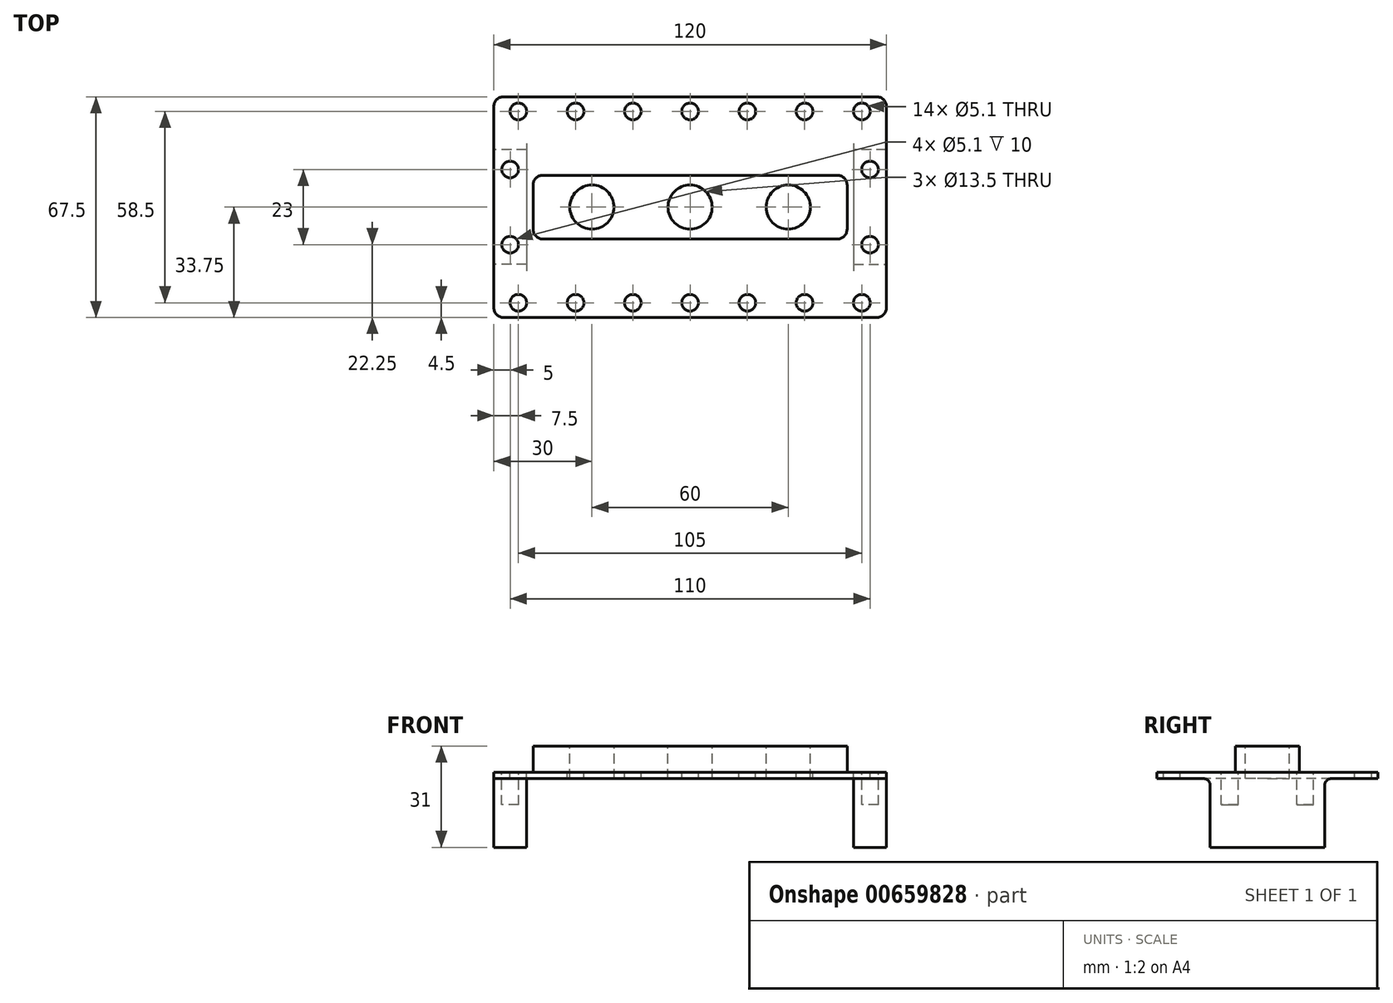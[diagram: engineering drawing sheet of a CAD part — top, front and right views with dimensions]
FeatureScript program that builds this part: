
annotation { "Feature Type Name" : "Feature", "Feature Type Description" : "" }
export const myFeature = defineFeature(function(context is Context, id is Id, definition is map)
    precondition{}
    {
        {
            var Q0;
            Q0=qCreatedBy(makeId("Top.planeOp"),FACE);
            var sketch = newSketch(context, id + "F0", { "sketchPlane" : qUnion([Q0])});
            skLineSegment(sketch, "E0.bottom", {"start": v(0, 0) * mm, "end": v(120, 0) * mm});
            skLineSegment(sketch, "E0.top", {"start": v(0, -67.5) * mm, "end": v(120, -67.5) * mm});
            skLineSegment(sketch, "E0.left", {"start": v(0, 0) * mm, "end": v(0, -67.5) * mm});
            skLineSegment(sketch, "E0.right", {"start": v(120, 0) * mm, "end": v(120, -67.5) * mm});
            skSolve(sketch);
        }
        {
            var Q0;
            Q0 = qSketchRegion(id + "F0", true);
            extrude(context, id + "F1", {"entities" : qUnion([Q0]), "depth" : 20 * mm, "offsetDistance" : 25 * mm});
        }
        {
            var Q0;
            Q0=makeQuery(id+"F1.opExtrude","CAP_FACE",FACE,{"disambiguationData":[OSD([sQuery(id+"F0.wireOp",EDGE,"E0.bottom"),sQuery(id+"F0.wireOp",EDGE,"E0.top"),sQuery(id+"F0.wireOp",EDGE,"E0.left"),sQuery(id+"F0.wireOp",EDGE,"E0.right")])],"isStart":false});
            var sketch = newSketch(context, id + "F2", { "sketchPlane" : qUnion([Q0])});
            skLineSegment(sketch, "E1.bottom", {"start": v(108, -43.5) * mm, "end": v(12, -43.5) * mm});
            skLineSegment(sketch, "E1.top", {"start": v(108, -24) * mm, "end": v(12, -24) * mm});
            skLineSegment(sketch, "E1.left", {"start": v(108, -43.5) * mm, "end": v(108, -24) * mm});
            skLineSegment(sketch, "E1.right", {"start": v(12, -43.5) * mm, "end": v(12, -24) * mm});
            skSolve(sketch);
        }
        {
            var Q0;
            Q0 = qSketchRegion(id + "F2", true);
            extrude(context, id + "F3", {"entities" : qUnion([Q0]), "operationType" : NewBodyOperationType.ADD, "depth" : 8 * mm, "offsetDistance" : 25 * mm});
        }
        {
            var Q0;
            Q0=makeQuery(id+"F3.opExtrude","CAP_FACE",FACE,{"disambiguationData":[OSD([sQuery(id+"F2.wireOp",EDGE,"E1.bottom"),sQuery(id+"F2.wireOp",EDGE,"E1.top"),sQuery(id+"F2.wireOp",EDGE,"E1.left"),sQuery(id+"F2.wireOp",EDGE,"E1.right")])],"isStart":false});
            var sketch = newSketch(context, id + "F4", { "sketchPlane" : qUnion([Q0])});
            skCircle(sketch, "E2", {"center": v(60, -33.75) * mm, "radius": 6.75 * mm});
            skCircle(sketch, "E3", {"center": v(30, -33.75) * mm, "radius": 6.75 * mm});
            skCircle(sketch, "E4", {"center": v(90, -33.75) * mm, "radius": 6.75 * mm});
            skSolve(sketch);
        }
        {
            var Q0;
            Q0 = qSketchRegion(id + "F4", true);
            extrude(context, id + "F5", {"entities" : qUnion([Q0]), "operationType" : NewBodyOperationType.REMOVE, "oppositeDirection" : true, "depth" : 25 * mm, "offsetDistance" : 25 * mm});
        }
        {
            var Q0;
            Q0=makeQuery(id+"F1.opExtrude","CAP_FACE",FACE,{"disambiguationData":[OSD([sQuery(id+"F0.wireOp",EDGE,"E0.bottom"),sQuery(id+"F0.wireOp",EDGE,"E0.top"),sQuery(id+"F0.wireOp",EDGE,"E0.left"),sQuery(id+"F0.wireOp",EDGE,"E0.right")])],"isStart":true});
            var sketch = newSketch(context, id + "F6", { "sketchPlane" : qUnion([Q0])});
            skLineSegment(sketch, "E5.bottom", {"start": v(110, 0) * mm, "end": v(10, 0) * mm});
            skLineSegment(sketch, "E5.top", {"start": v(110, 67.5) * mm, "end": v(10, 67.5) * mm});
            skLineSegment(sketch, "E5.left", {"start": v(110, 16.25) * mm, "end": v(110, 51.25) * mm});
            skLineSegment(sketch, "E5.right", {"start": v(10, 16.25) * mm, "end": v(10, 51.25) * mm});
            skLineSegment(sketch, "E6.bottom", {"start": v(10, 67.5) * mm, "end": v(0, 67.5) * mm});
            skLineSegment(sketch, "E6.top", {"start": v(10, 51.25) * mm, "end": v(0, 51.25) * mm});
            skLineSegment(sketch, "E6.right", {"start": v(0, 67.5) * mm, "end": v(0, 51.25) * mm});
            skLineSegment(sketch, "E7.bottom", {"start": v(110, 67.5) * mm, "end": v(120, 67.5) * mm});
            skLineSegment(sketch, "E7.top", {"start": v(110, 51.25) * mm, "end": v(120, 51.25) * mm});
            skLineSegment(sketch, "E7.right", {"start": v(120, 67.5) * mm, "end": v(120, 51.25) * mm});
            skLineSegment(sketch, "E8.bottom", {"start": v(120, 0) * mm, "end": v(0, 0) * mm});
            skLineSegment(sketch, "E8.top", {"start": v(120, 16.25) * mm, "end": v(110, 16.25) * mm});
            skLineSegment(sketch, "E8.left", {"start": v(120, 0) * mm, "end": v(120, 16.25) * mm});
            skLineSegment(sketch, "E8.right", {"start": v(0, 0) * mm, "end": v(0, 16.25) * mm});
            skLineSegment(sketch, "E9.trimOffspring", {"start": v(10, 16.25) * mm, "end": v(0, 16.25) * mm});
            skSolve(sketch);
        }
        {
            var Q0;
            Q0 = qSketchRegion(id + "F6", true);
            extrude(context, id + "F7", {"entities" : qUnion([Q0]), "operationType" : NewBodyOperationType.REMOVE, "oppositeDirection" : true, "depth" : 18 * mm, "offsetDistance" : 25 * mm});
        }
        {
            var Q0;
            {var subQ0=sQuery(id+"F0.wireOp",EDGE,"E0.right");var subQ1=sQuery(id+"F0.wireOp",EDGE,"E0.left");var subQ2=sQuery(id+"F0.wireOp",EDGE,"E0.top");var subQ3=sQuery(id+"F0.wireOp",EDGE,"E0.bottom");Q0=makeQuery(id+"FS7BLC4wZK1Tqsr_1.boolean.opBoolean","SPLIT",FACE,{"disambiguationData":[TD([makeQuery(id+"F1.opExtrude","SWEPT_FACE",FACE,{"disambiguationData":[OSD([subQ3])]})])],"derivedFrom":makeQuery(id+"F1.opExtrude","CAP_FACE",FACE,{"disambiguationData":[OSD([subQ3,subQ2,subQ1,subQ0])],"isStart":false})});}
            var sketch = newSketch(context, id + "F8", { "sketchPlane" : qUnion([Q0])});
            skCircle(sketch, "E10", {"center": v(7.5, -4.5) * mm, "radius": 2.55 * mm});
            skCircle(sketch, "E11.0.1.0", {"center": v(7.5, -63) * mm, "radius": 2.55 * mm});
            skCircle(sketch, "E11.1.0.0", {"center": v(25, -4.5) * mm, "radius": 2.55 * mm});
            skCircle(sketch, "E11.1.1.0", {"center": v(25, -63) * mm, "radius": 2.55 * mm});
            skCircle(sketch, "E11.2.0.0", {"center": v(42.5, -4.5) * mm, "radius": 2.55 * mm});
            skCircle(sketch, "E11.2.1.0", {"center": v(42.5, -63) * mm, "radius": 2.55 * mm});
            skCircle(sketch, "E11.3.0.0", {"center": v(60, -4.5) * mm, "radius": 2.55 * mm});
            skCircle(sketch, "E11.3.1.0", {"center": v(60, -63) * mm, "radius": 2.55 * mm});
            skCircle(sketch, "E11.4.0.0", {"center": v(77.5, -4.5) * mm, "radius": 2.55 * mm});
            skCircle(sketch, "E11.4.1.0", {"center": v(77.5, -63) * mm, "radius": 2.55 * mm});
            skCircle(sketch, "E11.5.0.0", {"center": v(95, -4.5) * mm, "radius": 2.55 * mm});
            skCircle(sketch, "E11.5.1.0", {"center": v(95, -63) * mm, "radius": 2.55 * mm});
            skCircle(sketch, "E11.6.0.0", {"center": v(112.5, -4.5) * mm, "radius": 2.55 * mm});
            skCircle(sketch, "E11.6.1.0", {"center": v(112.5, -63) * mm, "radius": 2.55 * mm});
            skLineSegment(sketch, "E11.direction1", {"start": v(7.5, -4.5) * mm, "end": v(25, -4.5) * mm, "construction": true});
            skLineSegment(sketch, "E11.direction2", {"start": v(7.5, -4.5) * mm, "end": v(7.5, -63) * mm, "construction": true});
            skSolve(sketch);
        }
        {
            var Q0;
            Q0 = qSketchRegion(id + "F8", true);
            extrude(context, id + "F9", {"entities" : qUnion([Q0]), "operationType" : NewBodyOperationType.REMOVE, "oppositeDirection" : true, "depth" : 25 * mm, "offsetDistance" : 25 * mm});
        }
        {
            var Q0;
            Q0=makeQuery(id+"F3.opExtrude","SWEPT_EDGE",EDGE,{"disambiguationData":[OSD([sQuery(id+"F2.wireOp",EDGE,"E1.bottom"),sQuery(id+"F2.wireOp",EDGE,"E1.left")])]});
            var Q1;
            Q1=makeQuery(id+"F3.opExtrude","SWEPT_EDGE",EDGE,{"disambiguationData":[OSD([sQuery(id+"F2.wireOp",EDGE,"E1.top"),sQuery(id+"F2.wireOp",EDGE,"E1.left")])]});
            var Q2;
            Q2=makeQuery(id+"F3.opExtrude","SWEPT_EDGE",EDGE,{"disambiguationData":[OSD([sQuery(id+"F2.wireOp",EDGE,"E1.top"),sQuery(id+"F2.wireOp",EDGE,"E1.right")])]});
            var Q3;
            Q3=makeQuery(id+"F3.opExtrude","SWEPT_EDGE",EDGE,{"disambiguationData":[OSD([sQuery(id+"F2.wireOp",EDGE,"E1.bottom"),sQuery(id+"F2.wireOp",EDGE,"E1.right")])]});
            fillet(context, id + "F10", {"entities" : qUnion([Q0, Q1, Q2, Q3]), "radius" : 3 * mm, "tangentPropagation" : true, "allowEdgeOverflow" : false});
        }
        {
            var Q0;
            Q0=makeQuery(id+"F1.opExtrude","SWEPT_EDGE",EDGE,{"disambiguationData":[OSD([sQuery(id+"F0.wireOp",EDGE,"E0.bottom"),sQuery(id+"F0.wireOp",EDGE,"E0.right")])]});
            var Q1;
            Q1=makeQuery(id+"F1.opExtrude","SWEPT_EDGE",EDGE,{"disambiguationData":[OSD([sQuery(id+"F0.wireOp",EDGE,"E0.top"),sQuery(id+"F0.wireOp",EDGE,"E0.right")])]});
            var Q2;
            Q2=makeQuery(id+"F1.opExtrude","SWEPT_EDGE",EDGE,{"disambiguationData":[OSD([sQuery(id+"F0.wireOp",EDGE,"E0.bottom"),sQuery(id+"F0.wireOp",EDGE,"E0.left")])]});
            var Q3;
            Q3=makeQuery(id+"F1.opExtrude","SWEPT_EDGE",EDGE,{"disambiguationData":[OSD([sQuery(id+"F0.wireOp",EDGE,"E0.top"),sQuery(id+"F0.wireOp",EDGE,"E0.left")])]});
            fillet(context, id + "F11", {"entities" : qUnion([Q0, Q1, Q2, Q3]), "radius" : 3 * mm, "tangentPropagation" : true, "allowEdgeOverflow" : false});
        }
        {
            var Q0;
            {var subQ0=sQuery(id+"F0.wireOp",EDGE,"E0.right");Q0=makeQuery(id+"F7.boolean.opBoolean","SPLIT",FACE,{"disambiguationData":[TD([makeQuery(id+"F1.opExtrude","SWEPT_FACE",FACE,{"disambiguationData":[OSD([subQ0])]})])],"derivedFrom":makeQuery(id+"F1.opExtrude","CAP_FACE",FACE,{"disambiguationData":[OSD([sQuery(id+"F0.wireOp",EDGE,"E0.bottom"),sQuery(id+"F0.wireOp",EDGE,"E0.top"),sQuery(id+"F0.wireOp",EDGE,"E0.left"),subQ0])],"isStart":true})});}
            var sketch = newSketch(context, id + "F12", { "sketchPlane" : qUnion([Q0])});
            skLineSegment(sketch, "E12.bottom", {"start": v(110, 16.25) * mm, "end": v(120, 16.25) * mm});
            skLineSegment(sketch, "E12.top", {"start": v(110, 51.25) * mm, "end": v(120, 51.25) * mm});
            skLineSegment(sketch, "E12.left", {"start": v(110, 16.25) * mm, "end": v(110, 51.25) * mm});
            skLineSegment(sketch, "E12.right", {"start": v(120, 16.25) * mm, "end": v(120, 51.25) * mm});
            skLineSegment(sketch, "E13.bottom", {"start": v(10, 16.25) * mm, "end": v(0, 16.25) * mm});
            skLineSegment(sketch, "E13.top", {"start": v(10, 51.25) * mm, "end": v(0, 51.25) * mm});
            skLineSegment(sketch, "E13.left", {"start": v(10, 16.25) * mm, "end": v(10, 51.25) * mm});
            skLineSegment(sketch, "E13.right", {"start": v(0, 16.25) * mm, "end": v(0, 51.25) * mm});
            skSolve(sketch);
        }
        {
            var Q0;
            Q0 = qSketchRegion(id + "F12", true);
            extrude(context, id + "F13", {"entities" : qUnion([Q0]), "operationType" : NewBodyOperationType.ADD, "depth" : 3 * mm, "offsetDistance" : 25 * mm});
        }
        {
            var Q0;
            Q0=makeQuery(id+"F7.boolean.opBoolean","COPY",EDGE,{"derivedFrom":makeQuery(id+"F7.opExtrude","CAP_EDGE",EDGE,{"disambiguationData":[OSD([sQuery(id+"F6.wireOp",EDGE,"E7.top")])],"isStart":false})});
            var Q1;
            Q1=makeQuery(id+"F7.boolean.opBoolean","COPY",EDGE,{"derivedFrom":makeQuery(id+"F7.opExtrude","CAP_EDGE",EDGE,{"disambiguationData":[OSD([sQuery(id+"F6.wireOp",EDGE,"E8.top")])],"isStart":false})});
            var Q2;
            Q2=makeQuery(id+"F7.boolean.opBoolean","COPY",EDGE,{"derivedFrom":makeQuery(id+"F7.opExtrude","CAP_EDGE",EDGE,{"disambiguationData":[OSD([sQuery(id+"F6.wireOp",EDGE,"E9.trimOffspring")])],"isStart":false})});
            var Q3;
            Q3=makeQuery(id+"F7.boolean.opBoolean","COPY",EDGE,{"derivedFrom":makeQuery(id+"F7.opExtrude","CAP_EDGE",EDGE,{"disambiguationData":[OSD([sQuery(id+"F6.wireOp",EDGE,"E6.top")])],"isStart":false})});
            fillet(context, id + "F14", {"entities" : qUnion([Q0, Q1, Q2, Q3]), "radius" : 2 * mm, "tangentPropagation" : true, "allowEdgeOverflow" : false});
        }
        {
            var Q0;
            Q0=makeQuery(id+"F1.opExtrude","CAP_FACE",FACE,{"disambiguationData":[OSD([sQuery(id+"F0.wireOp",EDGE,"E0.bottom"),sQuery(id+"F0.wireOp",EDGE,"E0.top"),sQuery(id+"F0.wireOp",EDGE,"E0.left"),sQuery(id+"F0.wireOp",EDGE,"E0.right")])],"isStart":false});
            var sketch = newSketch(context, id + "F15", { "sketchPlane" : qUnion([Q0])});
            skCircle(sketch, "E14", {"center": v(115, -22.25) * mm, "radius": 2.55 * mm});
            skCircle(sketch, "E15", {"center": v(115, -45.25) * mm, "radius": 2.55 * mm});
            skCircle(sketch, "E16.1.0.0", {"center": v(5, -45.25) * mm, "radius": 2.55 * mm});
            skCircle(sketch, "E16.1.0.1", {"center": v(5, -22.25) * mm, "radius": 2.55 * mm});
            skLineSegment(sketch, "E16.direction1", {"start": v(115, -45.25) * mm, "end": v(5, -45.25) * mm, "construction": true});
            skSolve(sketch);
        }
        {
            var Q0;
            Q0 = qSketchRegion(id + "F15", true);
            extrude(context, id + "F16", {"entities" : qUnion([Q0]), "operationType" : NewBodyOperationType.REMOVE, "oppositeDirection" : true, "depth" : 10 * mm, "offsetDistance" : 25 * mm});
        }
    });
